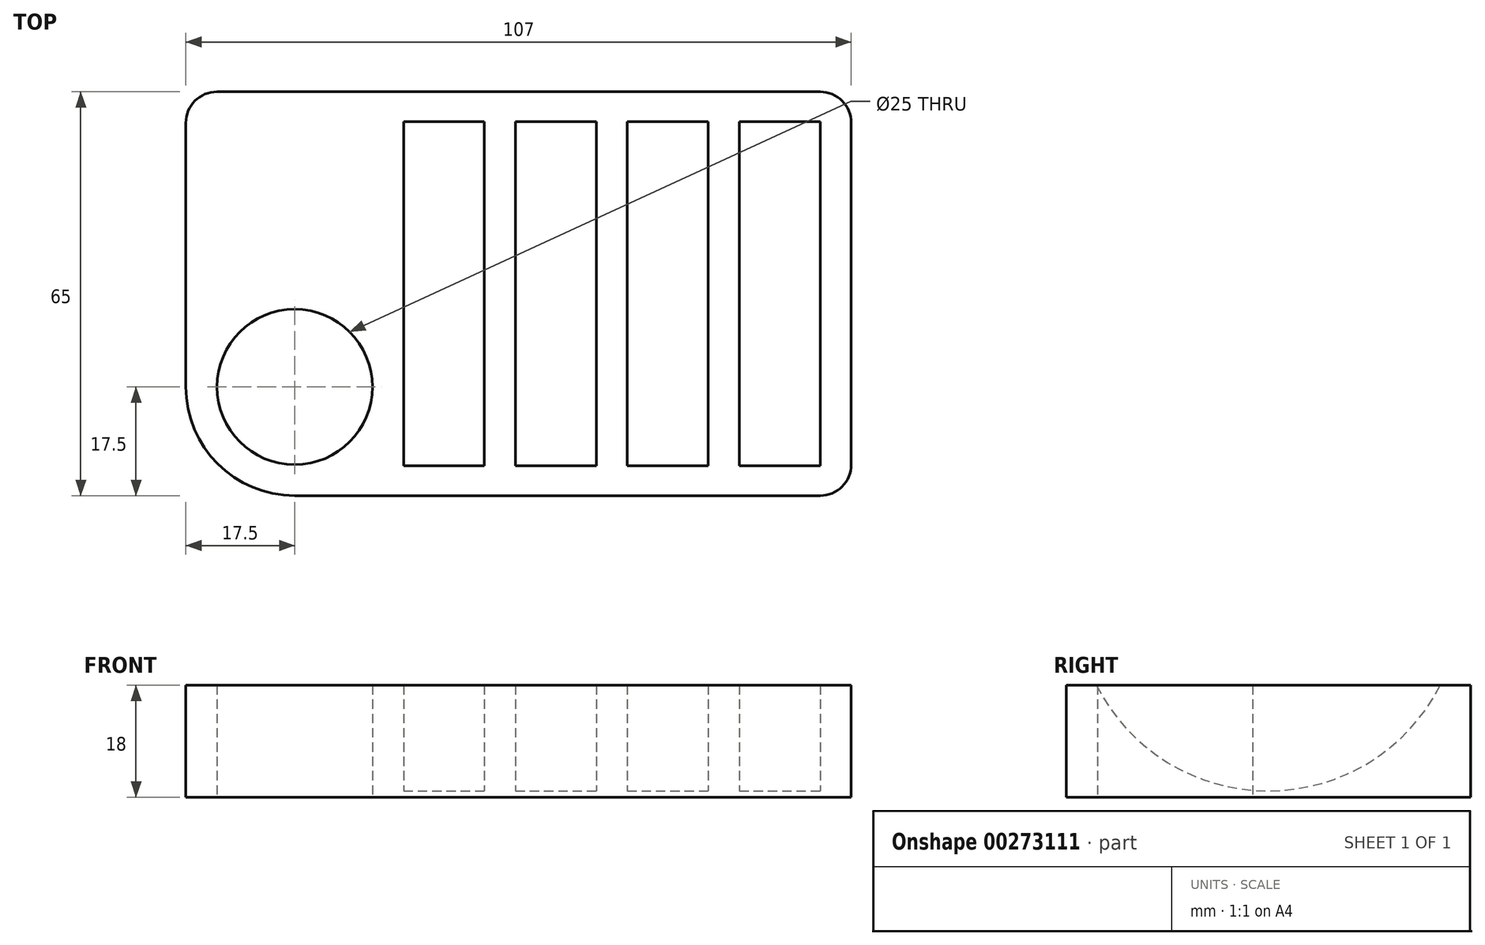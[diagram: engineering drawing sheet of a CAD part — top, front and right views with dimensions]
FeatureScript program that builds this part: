
annotation { "Feature Type Name" : "Feature", "Feature Type Description" : "" }
export const myFeature = defineFeature(function(context is Context, id is Id, definition is map)
    precondition{}
    {
        {
            var Q0;
            Q0=qCreatedBy(makeId("Top.planeOp"),FACE);
            var sketch = newSketch(context, id + "F0", { "sketchPlane" : qUnion([Q0])});
            skLineSegment(sketch, "E0.bottom", {"start": v(17.5, 0) * mm, "end": v(102, 0) * mm});
            skLineSegment(sketch, "E0.top", {"start": v(5, 65) * mm, "end": v(102, 65) * mm});
            skLineSegment(sketch, "E0.left", {"start": v(0, 17.5) * mm, "end": v(0, 60) * mm});
            skLineSegment(sketch, "E0.right", {"start": v(107, 5) * mm, "end": v(107, 60) * mm});
            skLineSegment(sketch, "E1.bottom", {"start": v(0, 0) * mm, "end": v(17.5, 0) * mm, "construction": true});
            skLineSegment(sketch, "E1.top", {"start": v(0, 17.5) * mm, "end": v(17.5, 17.5) * mm, "construction": true});
            skLineSegment(sketch, "E1.left", {"start": v(0, 0) * mm, "end": v(0, 17.5) * mm, "construction": true});
            skLineSegment(sketch, "E1.right", {"start": v(17.5, 0) * mm, "end": v(17.5, 17.5) * mm, "construction": true});
            skCircle(sketch, "E2", {"center": v(17.5, 17.5) * mm, "radius": 12.5 * mm});
            skPoint(sketch, "E3.visualSharp", {"position": v(0, 0) * mm});
            skArc(sketch, "E3.filletArc", {"start": v(0, 17.5) * mm, "mid": v(5.13, 5.13) * mm, "end": v(17.5, 0) * mm});
            skPoint(sketch, "E4.visualSharp", {"position": v(0, 65) * mm});
            skArc(sketch, "E4.filletArc", {"start": v(5, 65) * mm, "mid": v(1.46, 63.54) * mm, "end": v(0, 60) * mm});
            skPoint(sketch, "E5.visualSharp", {"position": v(107, 65) * mm});
            skArc(sketch, "E5.filletArc", {"start": v(107, 60) * mm, "mid": v(105.54, 63.54) * mm, "end": v(102, 65) * mm});
            skPoint(sketch, "E6.visualSharp", {"position": v(107, 0) * mm});
            skArc(sketch, "E6.filletArc", {"start": v(102, 0) * mm, "mid": v(105.54, 1.46) * mm, "end": v(107, 5) * mm});
            skSolve(sketch);
        }
        {
            var Q0;
            Q0=makeQuery(id+"F0.imprint","IMPRINT",FACE,{"disambiguationData":[TD([[makeQuery(id+"F0.imprint","IMPRINT",EDGE,{"derivedFrom":sQuery(id+"F0.wireOp",EDGE,"E0.bottom")}),1.0]])]});
            extrude(context, id + "F1", {"entities" : qUnion([Q0]), "depth" : 32 * mm});
        }
        {
            var Q0;
            Q0=makeQuery(id+"F1.opExtrude","CAP_FACE",FACE,{"disambiguationData":[OSD([sQuery(id+"F0.wireOp",EDGE,"E0.bottom"),sQuery(id+"F0.wireOp",EDGE,"E0.top"),sQuery(id+"F0.wireOp",EDGE,"E0.right"),sQuery(id+"F0.wireOp",EDGE,"E2"),sQuery(id+"F0.wireOp",EDGE,"E3.filletArc"),sQuery(id+"F0.wireOp",EDGE,"E4.filletArc"),sQuery(id+"F0.wireOp",EDGE,"E5.filletArc"),sQuery(id+"F0.wireOp",EDGE,"E6.filletArc")])],"isStart":false});
            var sketch = newSketch(context, id + "F2", { "sketchPlane" : qUnion([Q0])});
            skLineSegment(sketch, "E7.bottom", {"start": v(0, 0) * mm, "end": v(35, 0) * mm, "construction": true});
            skLineSegment(sketch, "E7.top", {"start": v(0, 32.5) * mm, "end": v(35, 32.5) * mm, "construction": true});
            skLineSegment(sketch, "E7.left", {"start": v(0, 0) * mm, "end": v(0, 32.5) * mm, "construction": true});
            skLineSegment(sketch, "E7.right", {"start": v(35, 0) * mm, "end": v(35, 32.5) * mm, "construction": true});
            skLineSegment(sketch, "E8.bottom", {"start": v(35, 32.5) * mm, "end": v(48, 32.5) * mm});
            skLineSegment(sketch, "E8.top", {"start": v(35, 1.5) * mm, "end": v(48, 1.5) * mm});
            skLineSegment(sketch, "E8.left", {"start": v(35, 32.5) * mm, "end": v(35, 1.5) * mm});
            skLineSegment(sketch, "E8.right", {"start": v(48, 32.5) * mm, "end": v(48, 1.5) * mm});
            skLineSegment(sketch, "E9", {"start": v(48, 32.5) * mm, "end": v(53, 32.5) * mm, "construction": true});
            skLineSegment(sketch, "E10.bottom", {"start": v(53, 32.5) * mm, "end": v(66, 32.5) * mm});
            skLineSegment(sketch, "E10.top", {"start": v(53, 1.5) * mm, "end": v(66, 1.5) * mm});
            skLineSegment(sketch, "E10.left", {"start": v(53, 32.5) * mm, "end": v(53, 1.5) * mm});
            skLineSegment(sketch, "E10.right", {"start": v(66, 32.5) * mm, "end": v(66, 1.5) * mm});
            skLineSegment(sketch, "E11", {"start": v(66, 32.5) * mm, "end": v(71, 32.5) * mm, "construction": true});
            skLineSegment(sketch, "E12.bottom", {"start": v(71, 32.5) * mm, "end": v(84, 32.5) * mm});
            skLineSegment(sketch, "E12.top", {"start": v(71, 1.5) * mm, "end": v(84, 1.5) * mm});
            skLineSegment(sketch, "E12.left", {"start": v(71, 32.5) * mm, "end": v(71, 1.5) * mm});
            skLineSegment(sketch, "E12.right", {"start": v(84, 32.5) * mm, "end": v(84, 1.5) * mm});
            skLineSegment(sketch, "E13", {"start": v(84, 32.5) * mm, "end": v(89, 32.5) * mm, "construction": true});
            skLineSegment(sketch, "E14.bottom", {"start": v(89, 32.5) * mm, "end": v(102, 32.5) * mm});
            skLineSegment(sketch, "E14.top", {"start": v(89, 1.5) * mm, "end": v(102, 1.5) * mm});
            skLineSegment(sketch, "E14.left", {"start": v(89, 32.5) * mm, "end": v(89, 1.5) * mm});
            skLineSegment(sketch, "E14.right", {"start": v(102, 32.5) * mm, "end": v(102, 1.5) * mm});
            skSolve(sketch);
        }
        {
            var Q0;
            Q0=makeQuery(id+"F2.imprint","IMPRINT",FACE,{"disambiguationData":[TD([[makeQuery(id+"F2.imprint","IMPRINT",EDGE,{"derivedFrom":sQuery(id+"F2.wireOp",EDGE,"E8.bottom")}),-1.0]])]});
            var Q1;
            Q1=makeQuery(id+"F2.imprint","IMPRINT",FACE,{"disambiguationData":[TD([[makeQuery(id+"F2.imprint","IMPRINT",EDGE,{"derivedFrom":sQuery(id+"F2.wireOp",EDGE,"E10.bottom")}),-1.0]])]});
            var Q2;
            Q2=makeQuery(id+"F2.imprint","IMPRINT",FACE,{"disambiguationData":[TD([[makeQuery(id+"F2.imprint","IMPRINT",EDGE,{"derivedFrom":sQuery(id+"F2.wireOp",EDGE,"E12.bottom")}),-1.0]])]});
            var Q3;
            Q3=makeQuery(id+"F2.imprint","IMPRINT",FACE,{"disambiguationData":[TD([[makeQuery(id+"F2.imprint","IMPRINT",EDGE,{"derivedFrom":sQuery(id+"F2.wireOp",EDGE,"E14.bottom")}),-1.0]])]});
            var Q4;
            Q4=sQuery(id+"F2.wireOp",EDGE,"E8.bottom");
            revolve(context, id + "F3", {"operationType" : NewBodyOperationType.REMOVE, "entities" : qUnion([Q0, Q1, Q2, Q3]), "axis" : qUnion([Q4]), "revolveType" : RevolveType.FULL, "oppositeDirection" : true});
        }
        {
            var Q0;
            Q0=makeQuery(id+"F1.opExtrude","SWEPT_FACE",FACE,{"disambiguationData":[OSD([sQuery(id+"F0.wireOp",EDGE,"E0.bottom")])]});
            var sketch = newSketch(context, id + "F4", { "sketchPlane" : qUnion([Q0])});
            skLineSegment(sketch, "E15", {"start": v(0, 0) * mm, "end": v(0, 18) * mm, "construction": true});
            skLineSegment(sketch, "E16.bottom", {"start": v(0, 18) * mm, "end": v(108.93, 18) * mm});
            skLineSegment(sketch, "E16.top", {"start": v(0, 36.1) * mm, "end": v(108.93, 36.1) * mm});
            skLineSegment(sketch, "E16.left", {"start": v(0, 18) * mm, "end": v(0, 36.1) * mm});
            skLineSegment(sketch, "E16.right", {"start": v(108.93, 18) * mm, "end": v(108.93, 36.1) * mm});
            skSolve(sketch);
        }
        {
            var Q0;
            Q0=qSketchRegion(id+"F4",true);
            extrude(context, id + "F5", {"entities" : qUnion([Q0]), "operationType" : NewBodyOperationType.REMOVE, "endBound" : BoundingType.THROUGH_ALL, "oppositeDirection" : true, "depth" : 25 * mm});
        }
    });
